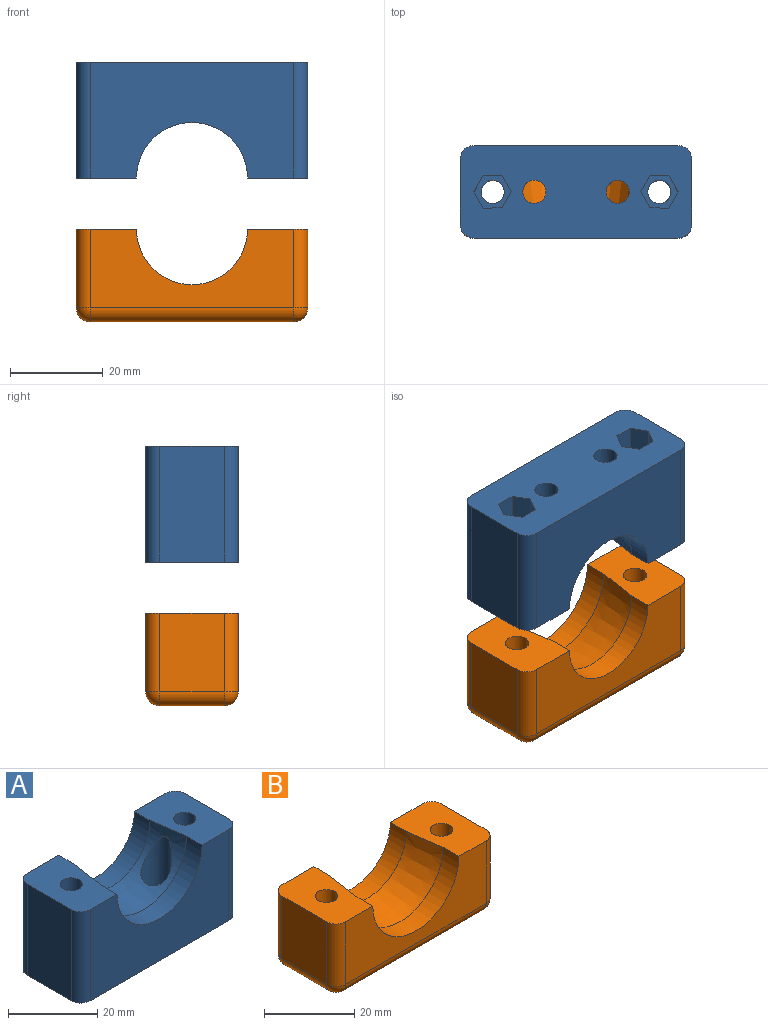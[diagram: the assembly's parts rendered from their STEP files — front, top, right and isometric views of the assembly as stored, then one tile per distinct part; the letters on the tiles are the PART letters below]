
ASSEMBLY  parts=2 mates=1
PART A: 36 faces, bbox 50x20x25 mm
  f0: cylinder r=2.5mm len=15mm, axis (0,0,-1), area 235.6mm2, adj f2,f24
  f1: cylinder r=2.5mm len=15mm, axis (0,0,-1), area 235.6mm2, adj f3,f17
  f2: plane 20x13mm, normal (0,0,1), area 221.5mm2, adj f0,f4,f5,f6,f8,f9,f10,f31
  f3: plane 20x13mm, normal (0,0,1), area 221.5mm2, adj f1,f4,f5,f7,f8,f9,f10,f33
  f4: plane 44x25mm, normal (0,1,0), area 873.8mm2, adj f2,f3,f9,f32,f33,f35
  f5: plane 44x25mm, normal (0,-1,0), area 813.7mm2, adj f2,f3,f8,f31,f34,f35
  f6: plane 25x14mm, normal (1,0,0), area 350mm2, adj f2,f31,f32,f35
  f7: plane 25x14mm, normal (-1,0,0), area 350mm2, adj f3,f33,f34,f35
  f8: cylinder r=13.5mm len=27mm, axis (0,-1,0), area 212.1mm2, adj f2,f3,f5,f10
  f9: cylinder r=12mm len=24mm, axis (0,1,0), area 188.5mm2, adj f2,f3,f4,f10
  f10: cone r=12mm half-angle=8.5deg, axis (0,-1,0), area 280.7mm2, adj f2,f3,f8,f9,f13,f15
  f11: cylinder r=2.5mm len=6mm, axis (0,0,-1), area 94.2mm2, adj f16,f35
  f12: cylinder r=2.5mm len=6mm, axis (0,0,-1), area 94.2mm2, adj f14,f35
  f13: cylinder r=3.5mm len=16.7mm, axis (0,0,-1), area 239.2mm2, adj f10,f14
  f14: plane 7x7mm, normal (0,0,1), area 18.8mm2, adj f12,f13
  f15: cylinder r=3.5mm len=16.7mm, axis (0,0,-1), area 239.2mm2, adj f10,f16
  f16: plane 7x7mm, normal (0,0,1), area 18.8mm2, adj f11,f15
  f17: plane 8.08x7.05mm, normal (0,0,-1), area 22.8mm2, adj f1,f18,f19,f20,f21,f22,f23
  f18: plane 10x3.48mm, normal (-0.86,0.51,0), area 40.4mm2, adj f17,f19,f23,f35
  f19: plane 10x4.04mm, normal (0.01,1,0), area 40.4mm2, adj f17,f18,f20,f35
  f20: plane 10x3.52mm, normal (0.87,0.49,0), area 40.4mm2, adj f17,f19,f21,f35
  f21: plane 10x3.48mm, normal (0.86,-0.51,0), area 40.4mm2, adj f17,f20,f22,f35
  f22: plane 10x4.04mm, normal (-0.01,-1,0), area 40.4mm2, adj f17,f21,f23,f35
  f23: plane 10x3.52mm, normal (-0.87,-0.49,0), area 40.4mm2, adj f17,f18,f22,f35
  f24: plane 8.08x7.05mm, normal (0,0,-1), area 22.8mm2, adj f0,f25,f26,f27,f28,f29,f30
  f25: plane 10x3.48mm, normal (0.86,0.51,0), area 40.4mm2, adj f24,f26,f30,f35
  f26: plane 10x3.52mm, normal (0.87,-0.49,0), area 40.4mm2, adj f24,f25,f27,f35
  f27: plane 10x4.04mm, normal (0.01,-1,0), area 40.4mm2, adj f24,f26,f28,f35
  f28: plane 10x3.48mm, normal (-0.86,-0.51,0), area 40.4mm2, adj f24,f27,f29,f35
  f29: plane 10x3.52mm, normal (-0.87,0.49,0), area 40.4mm2, adj f24,f28,f30,f35
  f30: plane 10x4.04mm, normal (-0.01,1,0), area 40.4mm2, adj f24,f25,f29,f35
  f31: cylinder r=3mm len=25mm, axis (0,0,1), area 117.8mm2, adj f2,f5,f6,f35
  f32: cylinder r=3mm len=25mm, axis (0,0,-1), area 117.8mm2, adj f2,f4,f6,f35
  f33: cylinder r=3mm len=25mm, axis (0,0,1), area 117.8mm2, adj f3,f4,f7,f35
  f34: cylinder r=3mm len=25mm, axis (0,0,-1), area 117.8mm2, adj f3,f5,f7,f35
  f35: plane 50x20mm, normal (0,0,-1), area 868.1mm2, adj f4,f5,f6,f7,f11,f12,f18,f19
PART B: 28 faces, bbox 50x20x20 mm
  f0: cylinder r=2.5mm len=15mm, axis (0,0,-1), area 235.6mm2, adj f2,f15
  f1: cylinder r=2.5mm len=15mm, axis (0,0,-1), area 235.6mm2, adj f3,f13
  f2: plane 20x13mm, normal (0,0,1), area 221.5mm2, adj f0,f4,f5,f6,f9,f10,f11,f18
  f3: plane 20x13mm, normal (0,0,1), area 221.5mm2, adj f1,f4,f5,f7,f9,f10,f11,f16
  f4: plane 44x17mm, normal (0,1,0), area 521.8mm2, adj f2,f3,f10,f16,f18,f19
  f5: plane 44x17mm, normal (0,-1,0), area 461.7mm2, adj f2,f3,f9,f21,f25,f27
  f6: plane 17x14mm, normal (1,0,0), area 238mm2, adj f2,f18,f24,f27
  f7: plane 17x14mm, normal (-1,0,0), area 238mm2, adj f3,f16,f20,f21
  f8: plane 44x14mm, normal (0,0,-1), area 503.5mm2, adj f12,f14,f19,f20,f24,f25
  f9: cylinder r=13.5mm len=27mm, axis (0,-1,0), area 212.1mm2, adj f2,f3,f5,f11
  f10: cylinder r=12mm len=24mm, axis (0,1,0), area 188.5mm2, adj f2,f3,f4,f11
  f11: cone r=12mm half-angle=8.5deg, axis (0,-1,0), area 405mm2, adj f2,f3,f9,f10
  f12: cylinder r=4.25mm len=8.5mm, axis (0,0,-1), area 133.5mm2, adj f8,f13,f20
  f13: plane 8.5x8.5mm, normal (0,0,-1), area 37.1mm2, adj f1,f12
  f14: cylinder r=4.25mm len=8.5mm, axis (0,0,-1), area 133.5mm2, adj f8,f15,f24
  f15: plane 8.5x8.5mm, normal (0,0,-1), area 37.1mm2, adj f0,f14
  f16: cylinder r=3mm len=17mm, axis (0,0,1), area 80.1mm2, adj f3,f4,f7,f17
  f17: sphere r=3mm, area 14.1mm2, adj f16,f19,f20
  f18: cylinder r=3mm len=17mm, axis (0,0,-1), area 80.1mm2, adj f2,f4,f6,f22
  f19: cylinder r=3mm len=44mm, axis (-1,0,0), area 207.3mm2, adj f4,f8,f17,f22
  f20: cylinder r=3mm len=14mm, axis (0,-1,0), area 65.5mm2, adj f7,f8,f12,f17,f23
  f21: cylinder r=3mm len=17mm, axis (0,0,-1), area 80.1mm2, adj f3,f5,f7,f23
  f22: sphere r=3mm, area 14.1mm2, adj f18,f19,f24
  f23: sphere r=3mm, area 14.1mm2, adj f20,f21,f25
  f24: cylinder r=3mm len=14mm, axis (0,1,0), area 65.5mm2, adj f6,f8,f14,f22,f26
  f25: cylinder r=3mm len=44mm, axis (1,0,0), area 207.3mm2, adj f5,f8,f23,f26
  f26: sphere r=3mm, area 14.1mm2, adj f24,f25,f27
  f27: cylinder r=3mm len=17mm, axis (0,0,1), area 80.1mm2, adj f2,f5,f6,f26
PLACE A rot(axis=(-1,0,0),180deg) t=(-33.67,-54.39,27.85)mm
PLACE B rot(axis=(0,0,-1),180deg) t=(-33.67,-54.39,-23.18)mm fixed
MATE slider A.f0 <-> B.f1  axis (0,0,-1) through (-15.67,-54.39,7.85)mm
